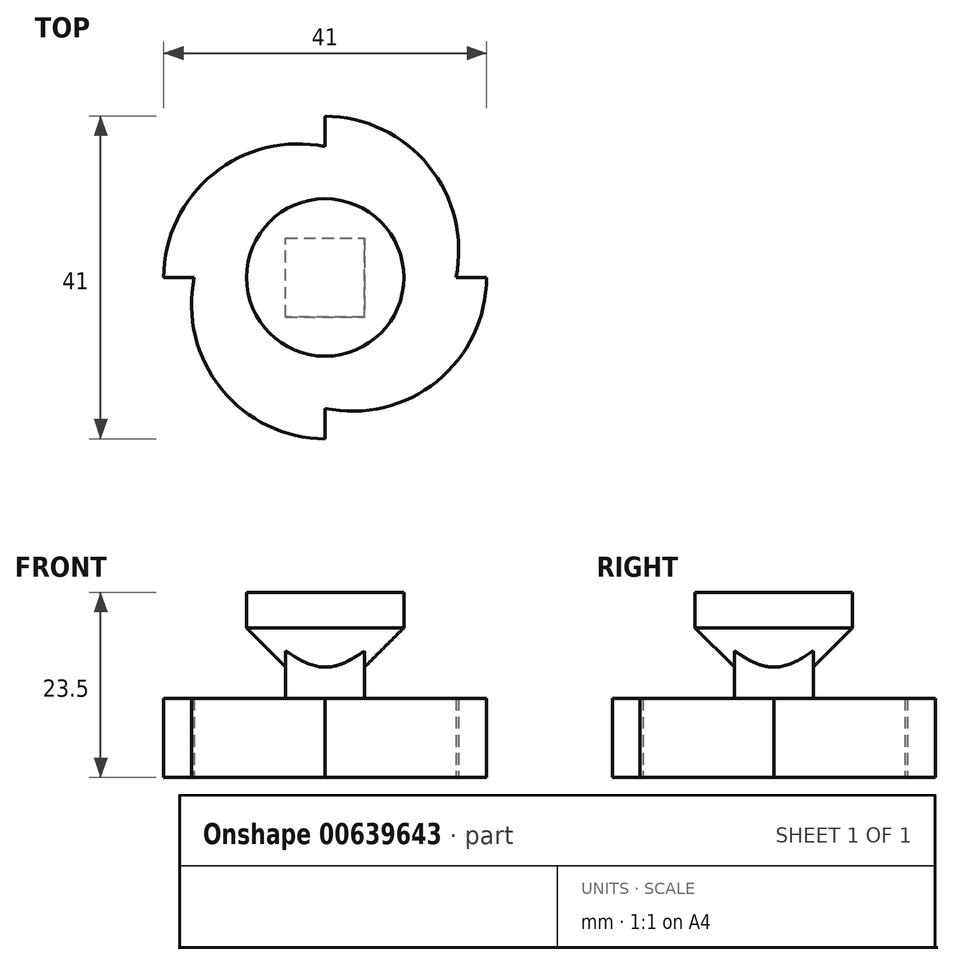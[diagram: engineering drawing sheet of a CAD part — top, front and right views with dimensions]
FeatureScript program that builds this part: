
annotation { "Feature Type Name" : "Feature", "Feature Type Description" : "" }
export const myFeature = defineFeature(function(context is Context, id is Id, definition is map)
    precondition{}
    {
        {
            var Q0;
            Q0=qCreatedBy(makeId("Top.planeOp"),FACE);
            var sketch = newSketch(context, id + "F0", { "sketchPlane" : qUnion([Q0])});
            skPoint(sketch, "E0.middle", {"position": v(0, 0) * mm});
            skLineSegment(sketch, "E1.bottom", {"start": v(5, 5) * mm, "end": v(-5, 5) * mm});
            skLineSegment(sketch, "E1.top", {"start": v(5, -5) * mm, "end": v(-5, -5) * mm});
            skLineSegment(sketch, "E1.left", {"start": v(5, 5) * mm, "end": v(5, -5) * mm});
            skLineSegment(sketch, "E1.right", {"start": v(-5, 5) * mm, "end": v(-5, -5) * mm});
            skLineSegment(sketch, "E2.bottom", {"start": v(-20.5, 20.5) * mm, "end": v(20.5, 20.5) * mm});
            skLineSegment(sketch, "E2.top", {"start": v(-20.5, -20.5) * mm, "end": v(20.5, -20.5) * mm});
            skLineSegment(sketch, "E2.left", {"start": v(-20.5, 20.5) * mm, "end": v(-20.5, -20.5) * mm});
            skLineSegment(sketch, "E2.right", {"start": v(20.5, 20.5) * mm, "end": v(20.5, -20.5) * mm});
            skSolve(sketch);
        }
        {
            var Q0;
            {var subQ1=sQuery(id+"F0.wireOp",EDGE,"E1.right");Q0=makeQuery(id+"F0.imprint","IMPRINT",FACE,{"disambiguationData":[TD([[makeQuery(id+"F0.imprint","IMPRINT",EDGE,{"derivedFrom":subQ1}),-1.0]])]});}
            var Q1;
            {var subQ1=sQuery(id+"F0.wireOp",EDGE,"E1.top");Q1=makeQuery(id+"F0.imprint","IMPRINT",FACE,{"disambiguationData":[TD([[makeQuery(id+"F0.imprint","IMPRINT",EDGE,{"derivedFrom":subQ1}),1.0]])]});}
            var Q2;
            {var subQ1=sQuery(id+"F0.wireOp",EDGE,"E1.left");Q2=makeQuery(id+"F0.imprint","IMPRINT",FACE,{"disambiguationData":[TD([[makeQuery(id+"F0.imprint","IMPRINT",EDGE,{"derivedFrom":subQ1}),1.0]])]});}
            var Q3;
            {var subQ5=sQuery(id+"F0.wireOp",EDGE,"E1.bottom");Q3=makeQuery(id+"F0.imprint","IMPRINT",FACE,{"disambiguationData":[TD([[makeQuery(id+"F0.imprint","IMPRINT",EDGE,{"derivedFrom":subQ5}),-1.0]])]});}
            var Q4;
            Q4=makeQuery(id+"F0.imprint","IMPRINT",FACE,{"disambiguationData":[TD([[makeQuery(id+"F0.imprint","IMPRINT",EDGE,{"derivedFrom":sQuery(id+"F0.wireOp",EDGE,"E1.bottom")}),1.0]])]});
            extrude(context, id + "F1", {"entities" : qUnion([Q0, Q1, Q2, Q3, Q4]), "depth" : 10 * mm, "offsetDistance" : 25 * mm});
        }
        {
            var Q0;
            Q0=makeQuery(id+"F0.imprint","IMPRINT",FACE,{"disambiguationData":[TD([[makeQuery(id+"F0.imprint","IMPRINT",EDGE,{"derivedFrom":sQuery(id+"F0.wireOp",EDGE,"E1.bottom")}),1.0]])]});
            extrude(context, id + "F2", {"entities" : qUnion([Q0]), "operationType" : NewBodyOperationType.ADD, "depth" : 25 * mm, "offsetDistance" : 25 * mm});
        }
        {
            var Q0;
            Q0=makeQuery(id+"F2.opExtrude","CAP_FACE",FACE,{"disambiguationData":[OSD([sQuery(id+"F0.wireOp",EDGE,"E1.bottom"),sQuery(id+"F0.wireOp",EDGE,"E1.top"),sQuery(id+"F0.wireOp",EDGE,"E1.left"),sQuery(id+"F0.wireOp",EDGE,"E1.right")])],"isStart":false});
            var sketch = newSketch(context, id + "F3", { "sketchPlane" : qUnion([Q0])});
            skLineSegment(sketch, "E3", {"start": v(-5, 5) * mm, "end": v(-5, -5) * mm});
            skPoint(sketch, "E4.middle", {"position": v(0, 0) * mm});
            skCircle(sketch, "E5", {"center": v(0, 0) * mm, "radius": 10 * mm});
            skSolve(sketch);
        }
        {
            var Q0;
            Q0 = qSketchRegion(id + "F3", true);
            extrude(context, id + "F4", {"entities" : qUnion([Q0]), "operationType" : NewBodyOperationType.ADD, "oppositeDirection" : true, "depth" : 8 * mm, "offsetDistance" : 25 * mm});
        }
        {
            var Q0;
            Q0=makeQuery(id+"F1.opExtrude","CAP_FACE",FACE,{"disambiguationData":[OSD([sQuery(id+"F0.wireOp",EDGE,"E2.bottom"),sQuery(id+"F0.wireOp",EDGE,"E2.top"),sQuery(id+"F0.wireOp",EDGE,"E2.left"),sQuery(id+"F0.wireOp",EDGE,"E2.right")])],"isStart":true});
            var sketch = newSketch(context, id + "F5", { "sketchPlane" : qUnion([Q0])});
            skLineSegment(sketch, "E6.bottom", {"start": v(5, 5) * mm, "end": v(-5, 5) * mm});
            skLineSegment(sketch, "E6.top", {"start": v(5, -5) * mm, "end": v(-5, -5) * mm});
            skLineSegment(sketch, "E6.left", {"start": v(5, 5) * mm, "end": v(5, -5) * mm});
            skLineSegment(sketch, "E6.right", {"start": v(-5, 5) * mm, "end": v(-5, -5) * mm});
            skPoint(sketch, "E6.middle", {"position": v(0, 0) * mm});
            skPoint(sketch, "E7", {"position": v(5, 5) * mm});
            skPoint(sketch, "E8", {"position": v(-5, 5) * mm});
            skPoint(sketch, "E9", {"position": v(-5, -5) * mm});
            skPoint(sketch, "E10", {"position": v(5, -5) * mm});
            skLineSegment(sketch, "E11", {"start": v(0, 16.62) * mm, "end": v(0, 20.5) * mm});
            skLineSegment(sketch, "E12", {"start": v(-16.62, 0) * mm, "end": v(-20.5, 0) * mm});
            skLineSegment(sketch, "E13", {"start": v(0, -16.62) * mm, "end": v(0, -20.5) * mm});
            skLineSegment(sketch, "E14", {"start": v(16.62, 0) * mm, "end": v(20.5, 0) * mm});
            skArc(sketch, "E15", {"start": v(0, -20.5) * mm, "mid": v(13.15, -14.18) * mm, "end": v(16.62, 0) * mm});
            skArc(sketch, "E16", {"start": v(20.5, 0) * mm, "mid": v(14.2, 13.18) * mm, "end": v(0, 16.62) * mm});
            skArc(sketch, "E17", {"start": v(0, 20.5) * mm, "mid": v(-13.16, 14.18) * mm, "end": v(-16.62, 0) * mm});
            skArc(sketch, "E18", {"start": v(-20.5, 0) * mm, "mid": v(-14.2, -13.17) * mm, "end": v(0, -16.62) * mm});
            skSolve(sketch);
        }
        {
            var Q0;
            {var subQ0=sQuery(id+"F5.wireOp",EDGE,"E11");Q0=makeQuery(id+"F5.imprint","IMPRINT",FACE,{"disambiguationData":[TD([[makeQuery(id+"F5.imprint","IMPRINT",EDGE,{"derivedFrom":subQ0}),-1.0]])]});}
            var Q1;
            {var subQ0=sQuery(id+"F5.wireOp",EDGE,"E14");Q1=makeQuery(id+"F5.imprint","IMPRINT",FACE,{"disambiguationData":[TD([[makeQuery(id+"F5.imprint","IMPRINT",EDGE,{"derivedFrom":subQ0}),-1.0]])]});}
            var Q2;
            {var subQ0=sQuery(id+"F5.wireOp",EDGE,"E13");Q2=makeQuery(id+"F5.imprint","IMPRINT",FACE,{"disambiguationData":[TD([[makeQuery(id+"F5.imprint","IMPRINT",EDGE,{"derivedFrom":subQ0}),-1.0]])]});}
            var Q3;
            {var subQ0=sQuery(id+"F5.wireOp",EDGE,"E12");Q3=makeQuery(id+"F5.imprint","IMPRINT",FACE,{"disambiguationData":[TD([[makeQuery(id+"F5.imprint","IMPRINT",EDGE,{"derivedFrom":subQ0}),-1.0]])]});}
            extrude(context, id + "F6", {"entities" : qUnion([Q0, Q1, Q2, Q3]), "operationType" : NewBodyOperationType.REMOVE, "oppositeDirection" : true, "depth" : 25 * mm, "offsetDistance" : 25 * mm});
        }
        {
            var Q0;
            Q0=makeQuery(id+"F4.boolean.opBoolean","MERGE",FACE,{"derivedFrom":[makeQuery(id+"F2.opExtrude","CAP_FACE",FACE,{"disambiguationData":[OSD([sQuery(id+"F0.wireOp",EDGE,"E1.bottom"),sQuery(id+"F0.wireOp",EDGE,"E1.top"),sQuery(id+"F0.wireOp",EDGE,"E1.left"),sQuery(id+"F0.wireOp",EDGE,"E1.right")])],"isStart":false}),makeQuery(id+"F4.opExtrude","CAP_FACE",FACE,{"disambiguationData":[OSD([sQuery(id+"F3.wireOp",EDGE,"E5")])],"isStart":true})]});
            extrude(context, id + "F7", {"entities" : qUnion([Q0]), "operationType" : NewBodyOperationType.REMOVE, "oppositeDirection" : true, "depth" : 1.5 * mm, "offsetDistance" : 25 * mm});
        }
        {
            var Q0;
            Q0=makeQuery(id+"F4.opExtrude","CAP_FACE",FACE,{"disambiguationData":[OSD([sQuery(id+"F3.wireOp",EDGE,"E5")])],"isStart":false});
            extrude(context, id + "F8", {"entities" : qUnion([Q0]), "operationType" : NewBodyOperationType.ADD, "depth" : 3 * mm, "offsetDistance" : 25 * mm});
        }
        {
            var Q0;
            Q0=makeQuery(id+"F8.opExtrude","CAP_EDGE",EDGE,{"disambiguationData":[OSD([sQuery(id+"F3.wireOp",EDGE,"E5")])],"isStart":false});
            chamfer(context, id + "F9", {"entities" : qUnion([Q0]), "width" : 5 * mm, "tangentPropagation" : true});
        }
    });
